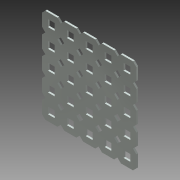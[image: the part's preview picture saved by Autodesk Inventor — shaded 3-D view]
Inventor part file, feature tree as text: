
AUTODESK INVENTOR PART (.ipt)
format: ipt  version: 2013 (Build 170138000, 138)  size: 350,208 bytes
history: native  units: mm (DEFAULTED — no unit token found)
features: other x26, extrude x25, pattern_linear x3, sketch x2, sheet_metal_op x1
ambient origin geometry x8: Origin, YZ Plane, XZ Plane, XY Plane, X Axis, Y Axis, Z Axis, Center Point
bodies: Solid1 (feature_tree)
feature tree (57):
  sheet_metal_op  "Face1"
  pattern_linear  "Rectangular Pattern1"  Spacing1=2.280986mm  [1 undecoded]
  pattern_linear  "Rectangular Pattern2"  Spacing1=2.280986mm  [1 undecoded]
  pattern_linear  "Rectangular Pattern3"  Spacing1=2.280986mm  [1 undecoded]
  sketch  "Sketch1"  dims[d0=12.7mm]
  other  "Plate1"
  sketch  "Sketch2"  dims[d1=12.7mm d2=2.280986mm d3=2.280986mm d4=2.280986mm d5=2.280986mm d6=2.280986mm d7=2.280986mm d8=2.280986mm d9=2.280986mm d10=4.572mm d11=4.572mm d12=4.064mm d13=4.064mm d14=1.1684mm d15=50.0mm d17=12.7mm d18=50.0mm d20=12.7mm d21=25.4mm d22=0.0mm d23=50.0mm d25=12.7mm d26=50.0mm d28=12.7mm d29=0.0mm d30=0.0mm d31=0.0mm d32=0.0mm d33=0.0mm d34=0.0mm d35=0.0mm d36=0.0mm d37=0.0mm d38=0.0mm d39=0.0mm d40=0.0mm d41=0.0mm d42=0.0mm d43=0.0mm d44=0.0mm d45=0.0mm d46=0.0mm d47=0.0mm d48=0.0mm d49=0.0mm d50=0.0mm d51=0.0mm d52=0.0mm d53=0.0mm d54=0.0mm d55=0.0mm d56=0.0mm d61=0.0mm d62=0.0mm d119=0.0mm d120=0.0mm d121=0.0mm d122=0.0mm d123=0.0mm d124=0.0mm d125=0.0mm d126=0.0mm d127=0.0mm d128=0.0mm d129=0.0mm d130=0.0mm d131=0.0mm d132=0.0mm d133=0.0mm d134=0.0mm d135=0.0mm d136=0.0mm d137=0.0mm d138=0.0mm]
  other  "Srf1"
  other  "Srf2"
  other  "Srf3"
  other  "Srf4"
  other  "Srf5"
  other  "Srf16"
  other  "Srf17"
  other  "Srf18"
  other  "Srf19"
  other  "Srf20"
  other  "Srf31"
  other  "Srf32"
  other  "Srf33"
  other  "Srf34"
  other  "Srf35"
  other  "Srf46"
  other  "Srf47"
  other  "Srf48"
  other  "Srf49"
  other  "Srf50"
  other  "Srf61"
  other  "Srf62"
  other  "Srf63"
  other  "Srf64"
  other  "Srf65"
  extrude  "ExtrusionSrf1"  Depth=2.280986mm
  extrude  "ExtrusionSrf2"  Depth=2.280986mm
  extrude  "ExtrusionSrf3"  Depth=2.280986mm
  extrude  "ExtrusionSrf4"  Depth=2.280986mm
  extrude  "ExtrusionSrf5"  Depth=2.280986mm
  extrude  "ExtrusionSrf16"  Depth=4.572mm
  extrude  "ExtrusionSrf17"  Depth=4.572mm
  extrude  "ExtrusionSrf18"  Depth=4.064mm
  extrude  "ExtrusionSrf19"  Depth=4.064mm
  extrude  "ExtrusionSrf20"  Depth=1.1684mm
  extrude  "ExtrusionSrf31"  Depth=50.0mm
  extrude  "ExtrusionSrf32"  Depth=50.0mm
  extrude  "ExtrusionSrf33"  Depth=25.4mm TaperAngle=0.0deg
  extrude  "ExtrusionSrf34"  Depth=50.0mm
  extrude  "ExtrusionSrf35"  TaperAngle=0.0deg  [1 undecoded]
  extrude  "ExtrusionSrf46"  TaperAngle=0.0deg  [1 undecoded]
  extrude  "ExtrusionSrf47"  TaperAngle=0.0deg  [1 undecoded]
  extrude  "ExtrusionSrf48"  TaperAngle=0.0deg  [1 undecoded]
  extrude  "ExtrusionSrf49"  TaperAngle=0.0deg  [1 undecoded]
  extrude  "ExtrusionSrf50"  TaperAngle=0.0deg  [1 undecoded]
  extrude  "ExtrusionSrf61"  TaperAngle=0.0deg  [1 undecoded]
  extrude  "ExtrusionSrf62"  TaperAngle=0.0deg  [1 undecoded]
  extrude  "ExtrusionSrf63"  TaperAngle=0.0deg  [1 undecoded]
  extrude  "ExtrusionSrf64"  TaperAngle=0.0deg  [1 undecoded]
  extrude  "ExtrusionSrf65"  TaperAngle=0.0deg  [1 undecoded]
note: 14 required parameter values undecoded (feature->parameter linkage not recoverable at this tier; creation-order binding heuristic only, values carry confidence <= 0.55)
